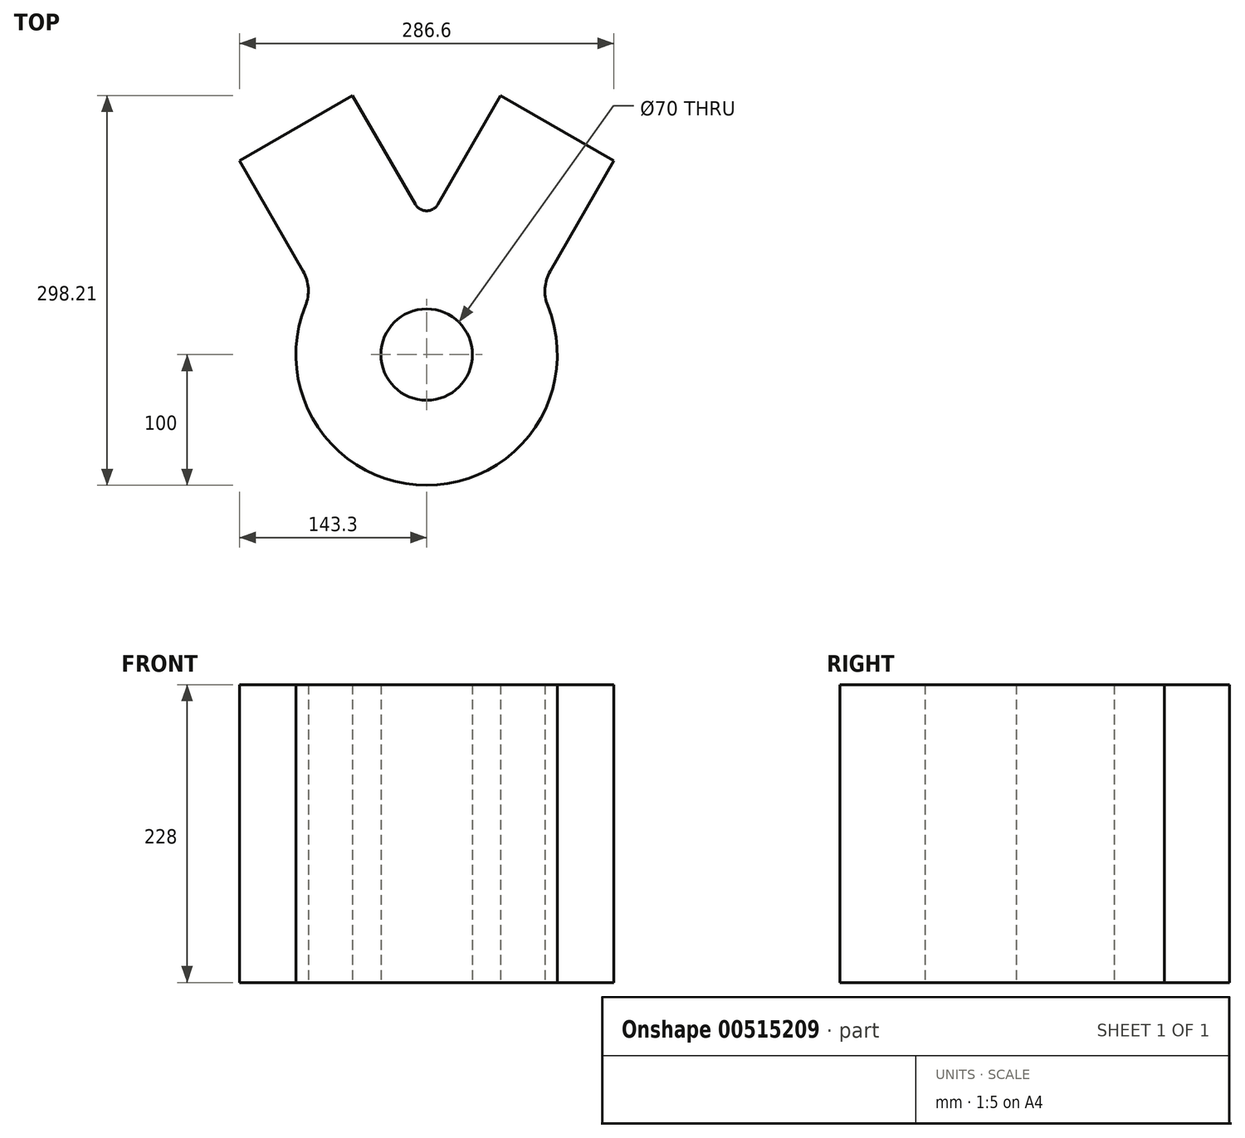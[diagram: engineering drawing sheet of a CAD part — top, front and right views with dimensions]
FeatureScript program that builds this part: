
annotation { "Feature Type Name" : "Feature", "Feature Type Description" : "" }
export const myFeature = defineFeature(function(context is Context, id is Id, definition is map)
    precondition{}
    {
        {
            var Q0;
            Q0=qCreatedBy(makeId("Top.planeOp"),FACE);
            var sketch = newSketch(context, id + "F0", { "sketchPlane" : qUnion([Q0])});
            skArc(sketch, "E0", {"start": v(92.7, 37.5) * mm, "mid": v(0, -100) * mm, "end": v(-92.7, 37.5) * mm});
            skLineSegment(sketch, "E1", {"start": v(-143.3, 148.2) * mm, "end": v(-56.7, 198.2) * mm});
            skLineSegment(sketch, "E2", {"start": v(-56.7, 198.2) * mm, "end": v(-8.66, 115) * mm});
            skLineSegment(sketch, "E3", {"start": v(143.3, 148.2) * mm, "end": v(56.7, 198.2) * mm});
            skLineSegment(sketch, "E4", {"start": v(56.7, 198.2) * mm, "end": v(8.66, 115) * mm});
            skArc(sketch, "E5", {"start": v(-8.66, 115) * mm, "mid": v(0, 110) * mm, "end": v(8.66, 115) * mm});
            skLineSegment(sketch, "E6", {"start": v(0, -138.28) * mm, "end": v(0, 272.02) * mm, "construction": true});
            skLineSegment(sketch, "E7", {"start": v(-143.3, 148.2) * mm, "end": v(-94.54, 63.74) * mm});
            skLineSegment(sketch, "E8", {"start": v(143.3, 148.2) * mm, "end": v(94.54, 63.74) * mm});
            skLineSegment(sketch, "E9", {"start": v(-114, 197.44) * mm, "end": v(0, 0) * mm, "construction": true});
            skLineSegment(sketch, "E10", {"start": v(114, 197.44) * mm, "end": v(0, 0) * mm, "construction": true});
            skArc(sketch, "E11", {"start": v(-92.7, 37.5) * mm, "mid": v(-90.59, 50.83) * mm, "end": v(-94.54, 63.74) * mm});
            skArc(sketch, "E12", {"start": v(94.54, 63.74) * mm, "mid": v(90.59, 50.83) * mm, "end": v(92.7, 37.5) * mm});
            skCircle(sketch, "E13", {"center": v(0, 0) * mm, "radius": 35 * mm});
            skSolve(sketch);
        }
        {
            var Q0;
            Q0 = qSketchRegion(id + "F0", true);
            extrude(context, id + "F1", {"entities" : qUnion([Q0]), "depth" : 228 * mm, "offsetDistance" : 25 * mm});
        }
    });
